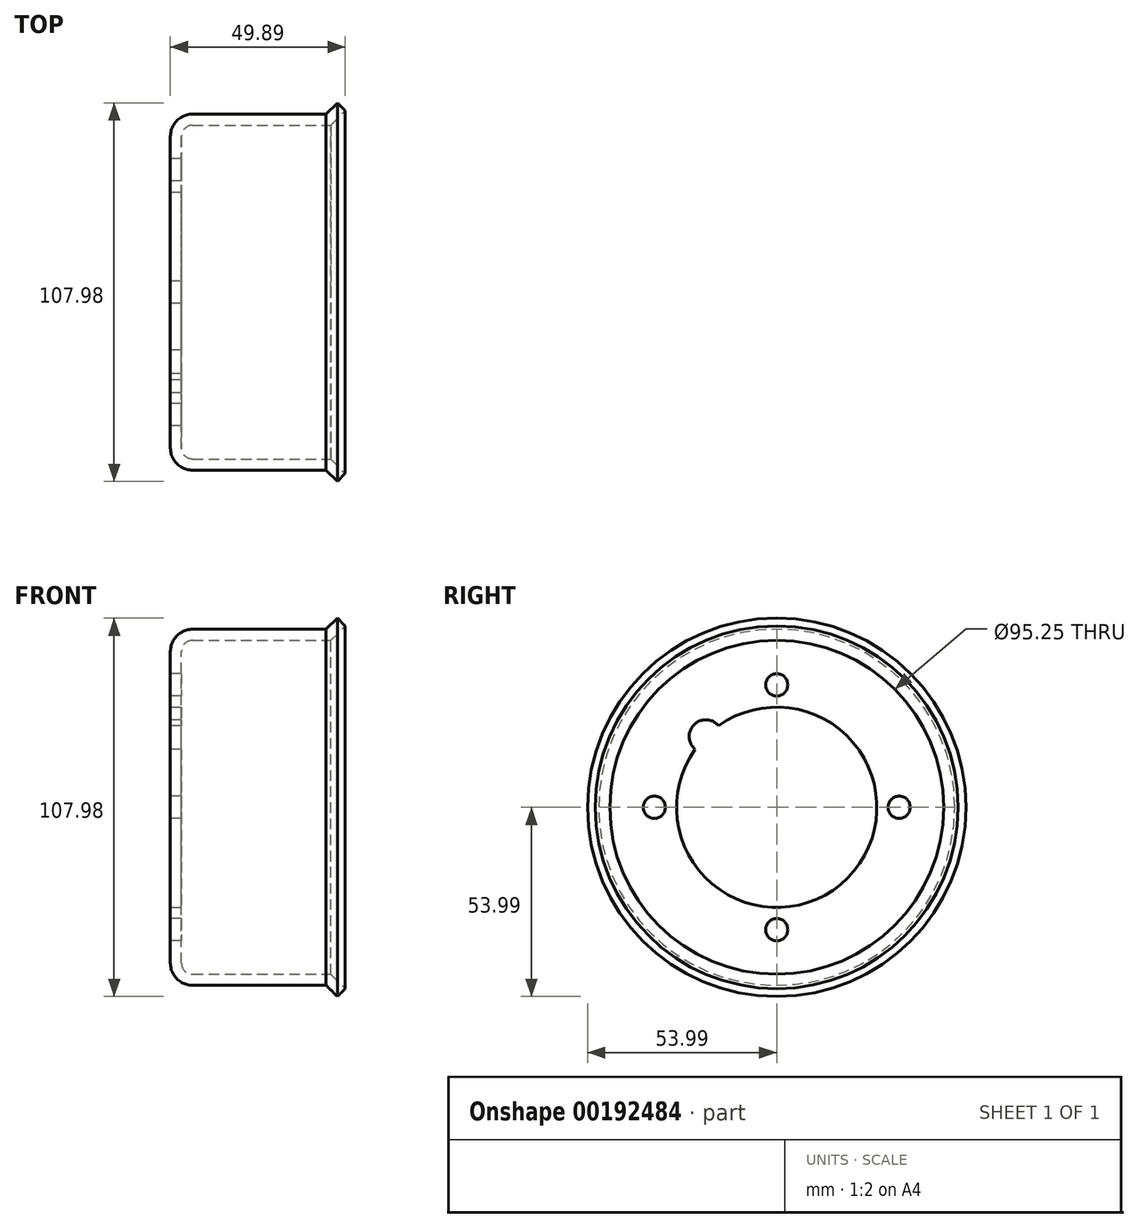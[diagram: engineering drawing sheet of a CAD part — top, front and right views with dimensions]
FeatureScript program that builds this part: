
annotation { "Feature Type Name" : "Feature", "Feature Type Description" : "" }
export const myFeature = defineFeature(function(context is Context, id is Id, definition is map)
    precondition{}
    {
        {
            var Q0;
            Q0=qCreatedBy(makeId("Front.planeOp"),FACE);
            var sketch = newSketch(context, id + "F0", { "sketchPlane" : qUnion([Q0])});
            skLineSegment(sketch, "E0.left", {"start": v(0, 44.45) * mm, "end": v(0, 28.58) * mm});
            skPoint(sketch, "E0.middle", {"position": v(0, 0) * mm});
            skLineSegment(sketch, "E1", {"start": v(-3.17, 28.58) * mm, "end": v(0, 28.58) * mm});
            skLineSegment(sketch, "E2", {"start": v(3.17, 47.63) * mm, "end": v(42.6, 47.63) * mm});
            skLineSegment(sketch, "E3", {"start": v(41.27, 50.8) * mm, "end": v(3.17, 50.8) * mm});
            skLineSegment(sketch, "E4", {"start": v(-3.18, 28.58) * mm, "end": v(-3.18, 44.45) * mm});
            skLineSegment(sketch, "E5", {"start": v(46.71, 51.75) * mm, "end": v(44.47, 54) * mm});
            skLineSegment(sketch, "E6", {"start": v(44.47, 54) * mm, "end": v(41.27, 50.8) * mm});
            skLineSegment(sketch, "E7", {"start": v(46.71, 51.75) * mm, "end": v(42.6, 47.63) * mm});
            skLineSegment(sketch, "E8", {"start": v(32.1, 0) * mm, "end": v(-37.8, 0) * mm, "construction": true});
            skPoint(sketch, "E9.visualSharp", {"position": v(0, 47.63) * mm});
            skArc(sketch, "E9.filletArc", {"start": v(3.17, 47.63) * mm, "mid": v(0.93, 46.7) * mm, "end": v(0, 44.45) * mm});
            skArc(sketch, "E10", {"start": v(3.17, 50.8) * mm, "mid": v(-1.32, 48.94) * mm, "end": v(-3.18, 44.45) * mm});
            skSolve(sketch);
        }
        {
            var Q0;
            Q0 = qSketchRegion(id + "F0", true);
            var Q1;
            Q1=sQuery(id+"F0.wireOp",EDGE,"E8");
            revolve(context, id + "F1", {"entities" : qUnion([Q0]), "axis" : qUnion([Q1]), "revolveType" : RevolveType.FULL});
        }
        {
            var Q0;
            Q0=qCreatedBy(makeId("Right.planeOp"),FACE);
            var sketch = newSketch(context, id + "F2", { "sketchPlane" : qUnion([Q0])});
            skCircle(sketch, "E11", {"center": v(0, 0) * mm, "radius": 34.93 * mm, "construction": true});
            skCircle(sketch, "E12", {"center": v(0, 34.93) * mm, "radius": 3.18 * mm});
            skCircle(sketch, "E13.1.0", {"center": v(-34.93, 0) * mm, "radius": 3.18 * mm});
            skCircle(sketch, "E13.2.0", {"center": v(0, -34.93) * mm, "radius": 3.18 * mm});
            skCircle(sketch, "E13.3.0", {"center": v(34.93, 0) * mm, "radius": 3.18 * mm});
            skLineSegment(sketch, "E14", {"start": v(0, 0) * mm, "end": v(-24.7, 24.7) * mm, "construction": true});
            skCircle(sketch, "E15", {"center": v(-20.2, 20.2) * mm, "radius": 4.76 * mm});
            skSolve(sketch);
        }
        {
            var Q0;
            Q0 = qSketchRegion(id + "F2", true);
            extrude(context, id + "F3", {"entities" : qUnion([Q0]), "operationType" : NewBodyOperationType.REMOVE, "endBound" : BoundingType.SYMMETRIC, "depth" : 6.35 * mm});
        }
    });
